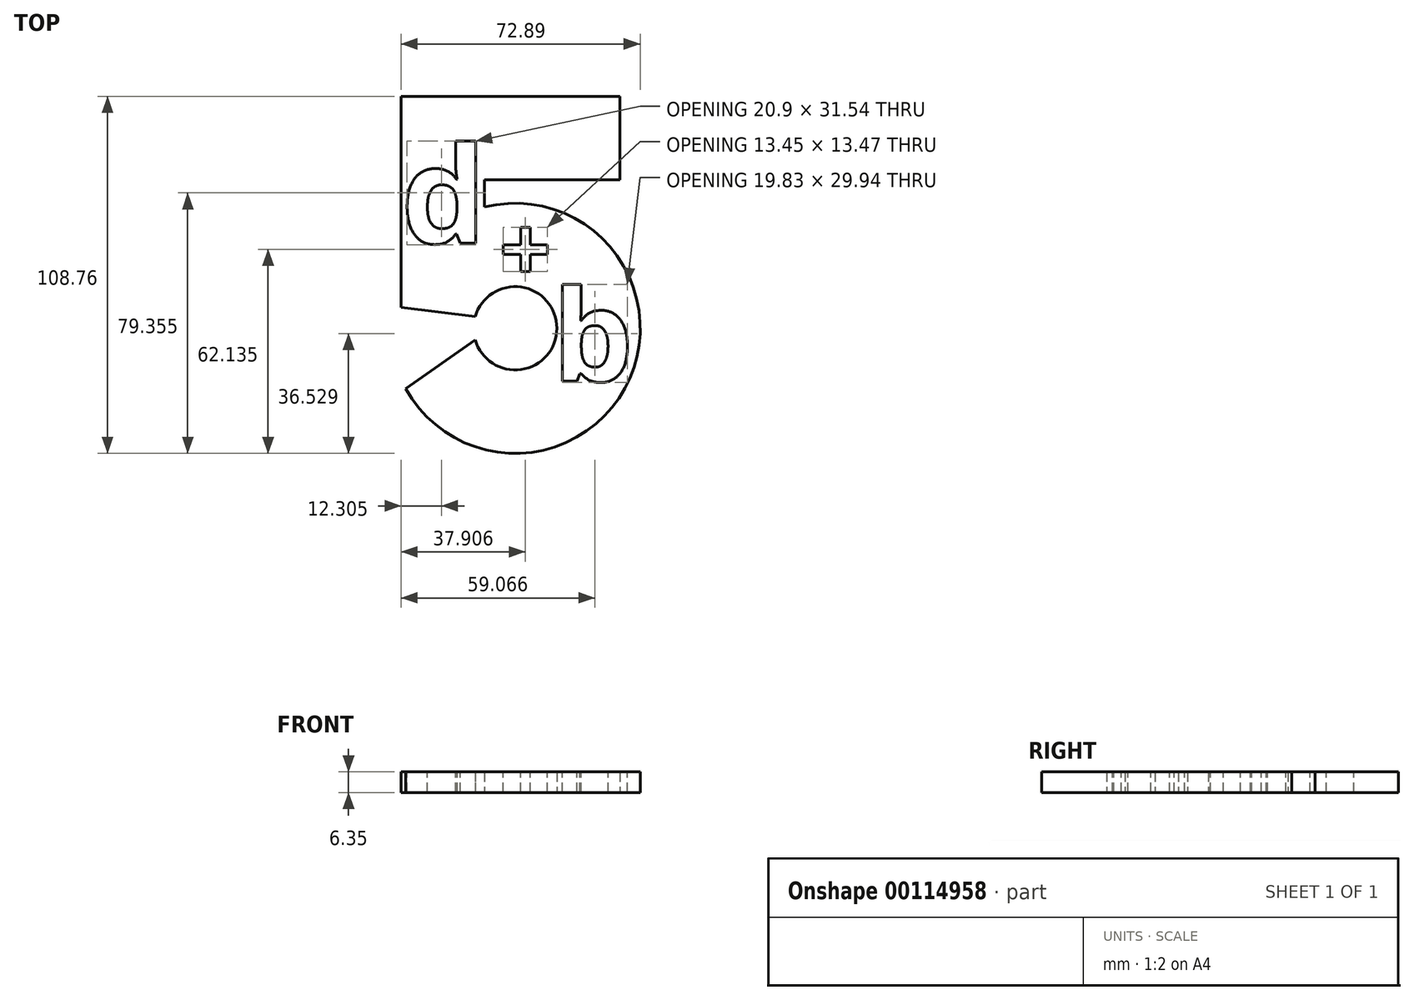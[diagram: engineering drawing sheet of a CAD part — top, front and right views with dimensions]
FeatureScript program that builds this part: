
annotation { "Feature Type Name" : "Feature", "Feature Type Description" : "" }
export const myFeature = defineFeature(function(context is Context, id is Id, definition is map)
    precondition{}
    {
        {
            var Q0;
            Q0=qCreatedBy(makeId("Top.planeOp"),FACE);
            var sketch = newSketch(context, id + "F0", { "sketchPlane" : qUnion([Q0])});
            skLineSegment(sketch, "E0", {"start": v(27.82, 58.49) * mm, "end": v(-38.9, 58.49) * mm});
            skLineSegment(sketch, "E1", {"start": v(-38.9, 58.49) * mm, "end": v(-38.9, -5.84) * mm});
            skLineSegment(sketch, "E2", {"start": v(27.82, 58.49) * mm, "end": v(27.82, 33.09) * mm});
            skLineSegment(sketch, "E3", {"start": v(27.82, 33.09) * mm, "end": v(-13.5, 33.09) * mm});
            skLineSegment(sketch, "E4", {"start": v(-13.5, 33.09) * mm, "end": v(-13.5, 24.75) * mm});
            skArc(sketch, "E5", {"start": v(-37.52, -30.51) * mm, "mid": v(30.82, -27.35) * mm, "end": v(-13.5, 24.75) * mm});
            skLineSegment(sketch, "E6", {"start": v(-38.9, -5.84) * mm, "end": v(-16.32, -8.62) * mm});
            skArc(sketch, "E7", {"start": v(-16.32, -15.73) * mm, "mid": v(8.58, -12.17) * mm, "end": v(-16.32, -8.62) * mm});
            skLineSegment(sketch, "E8", {"start": v(-16.32, -15.73) * mm, "end": v(-37.52, -30.51) * mm});
            skSolve(sketch);
        }
        {
            var Q0;
            Q0 = qSketchRegion(id + "F0", true);
            extrude(context, id + "F1", {"entities" : qUnion([Q0]), "depth" : 6.35 * mm});
        }
        {
            var Q0;
            Q0=makeQuery(id+"F1.opExtrude","CAP_FACE",FACE,{"disambiguationData":[OSD([sQuery(id+"F0.wireOp",EDGE,"E0"),sQuery(id+"F0.wireOp",EDGE,"E1"),sQuery(id+"F0.wireOp",EDGE,"E2"),sQuery(id+"F0.wireOp",EDGE,"E3"),sQuery(id+"F0.wireOp",EDGE,"E4"),sQuery(id+"F0.wireOp",EDGE,"E5"),sQuery(id+"F0.wireOp",EDGE,"E6"),sQuery(id+"F0.wireOp",EDGE,"E7"),sQuery(id+"F0.wireOp",EDGE,"E8")])],"isStart":false});
            var sketch = newSketch(context, id + "F2", { "sketchPlane" : qUnion([Q0])});
            skText(sketch, "E9", { "text": "d\n", "fontName": "OpenSans-Bold.ttf"});
            skText(sketch, "E10", { "text": "+", "fontName": "OpenSans-Bold.ttf"});
            skText(sketch, "E11", { "text": "b", "fontName": "OpenSans-Bold.ttf"});
            const initialGuessF2  = {"E9": [-0.0389, 0.01372, 1, 0, 0.0295], "E10": [-0.00892, 0.00206, 1, 0, 0.01997], "E11": [0.0072, -0.02833, 1, 0, 0.02801]};
            skSetInitialGuess(sketch, initialGuessF2);
            skSolve(sketch);
        }
        {
            var Q0;
            Q0 = qSketchRegion(id + "F2", true);
            extrude(context, id + "F3", {"entities" : qUnion([Q0]), "operationType" : NewBodyOperationType.REMOVE, "oppositeDirection" : true, "depth" : 25.4 * mm});
        }
    });
